# Revit family: c69f355d-e1fb-44ec-ac0f-3da983c7c191
name_source: partatom
category: Doors
revit_build: Autodesk Revit 2016 (Build: 20161004_0715(x64)
units: mm (PartAtom-declared; Revit-internal decimal feet)

## family parameters
Always vertical = Yes
Cut with Voids When Loaded = No
Host = Wall
OmniClass Number = 23.30.60.17.14
OmniClass Title = Smoke Curtains and Shutters
Room Calculation Point = No
Shared = No

## types (1)
- SmokeShield-Offset
    04 CSI = 08 34 83
    Analytic Construction = <None>
    Assembly Code = B2030410
    Bottom Bar = Metal - Steel - CornelIron - Steel - w - Powder Coated - Rust Inhibiting Paint
    CAD Resources = https://www.cornellIron.com
    Cornelliron Products = https://www.cornellIron.com
    Cornelliron Projects = https://www.cornellIron.com
    Cost Note = Based on size, materials selected. Consult CornellIron.
    Curtain = Curtain is composed of 0.002In thick transparent nylon film
    Curtain Film 2In OC Standard = CurtainControls - CornellIron
    Curtain Graphics = Clearly delineated emergency operation curtain mounted switch with the word “OPEN” on each side of curtain. Clearly delineated lift handle operational icon.
    Description = Alarm activated elevator door smoke containment system designed to seal the hoistway opening from smoke and air infiltration.
    Distance Between Guides = -7 1/4"
    Distributor Locator = https://www.cornelliron.com
    Edge Retention = Continuous formed strips mechanically interlocking to guide channel to provide complete curtain reseal after each cycle.
    Function = Interior
    Guides = Metal - Steel - CornelIron - Steel - w - Powder Coated - Rust Inhibiting Paint
    Head Box = 24 Gauge cold rolled powder coated steel housing, 20 gauge cold rolled powder coated steel mounting plat. Bottom access panel for control box, battery and motor.
    Height = 0"
    Height Note = Maximum 12ft wide and 12ft high
    Hood = Metal - Steel - CornelIron - Steel - w - Powder Coated - Rust Inhibiting Paint
    Jamb Dimension Note = Face of Wall: 2-1/4 inches (57.2 mm) wide; 1 inch deep. Consult Cornell when dimensions are critical.
    LEED Information = https://www.cornelliron.com
    Length Note = Distance Between Guides + 10.797
    Lift Strap = 3/16 inch (4.76mm) thick, 1 inch (25mm) wide nylon webbing, anchored to bottom bar and to curtain.
    Listings = UL 1784 Test Standard for Air Leakage; UL 325, ASTM E864. Complies with IBC 2003,2006, 2009, 2012, 2015, 2018.
    Manufacturer = CornellIron:  24 Elmwood Ave, Mountain Top, PA 18707.  Telephone: (800) 294-4358
    Model = SmokeShield® Elevator - Model # - ERF 10
    Motor Operator = 24V DC Motor and Controls, with standard battert back-up. Electrically activated by the [local smoke detector] [fire alarm control panel].
10 second time delay to close upon activation.Automatic reset when alarm cleared.Automatic curtain re-open on alarm clearance
    Mounting = Face of Wall - Offset or Over Frame with headerbox below or flush with ceiling
    Operation = 24V DC Motor and Controls, with standard battert back-up. Electrically activated by the [local smoke detector] [fire alarm control panel].
10 second time delay to close upon activation.Automatic reset when alarm cleared.Automatic curtain re-open on alarm clearance
    Operator Height = 64"
    Product Options = Wire directly to emergency back-up source
    Product Page = https://www.cornellIron.com
    Representative Disclaimer = CornellIron products are sold and installed through a nationwide network of independent distributors.
    Rough Height = 0"
    Sizing Disclaimer = Minimum openings of 3ft wide x 4ft high and Max openings up to 12ft wide x 12ft high standard construction. Consult Cornell for larger sizes. Exceeding maximum size may require UL approval.
    Smoke Control Windload = UL 1784 Test Standard for Air Leakage:  UL Listed. Not to exceed 3 cfm (0.001416 m3/s) per sf of door opening at 0.1 in (25 Pa) water pressure differential at ambient temperature and 400 degrees F (204 degrees C) tested per IBC 2006, 2009, and 2012, 2015
    Specifications = https://www.cornellIron.com
    Subcategory = Roll Up
    Type Image = <None>
    URL = https://www.cornellIron.com
    URL Photographs = https://www.cornelliron.com
    URL Specifications = https://www.cornelliron.com
    Wall Closure = By host
    Wall Construction = Drywall (steel or wood studs), structural steel, and masonry.
    Width = 36"
    Width Note = Minimum 3ft wide and 4ft high

## geometry (parser evidence)
native form markers: Blend x8, Sweep x14
no freeform markers — native parametric forms only
